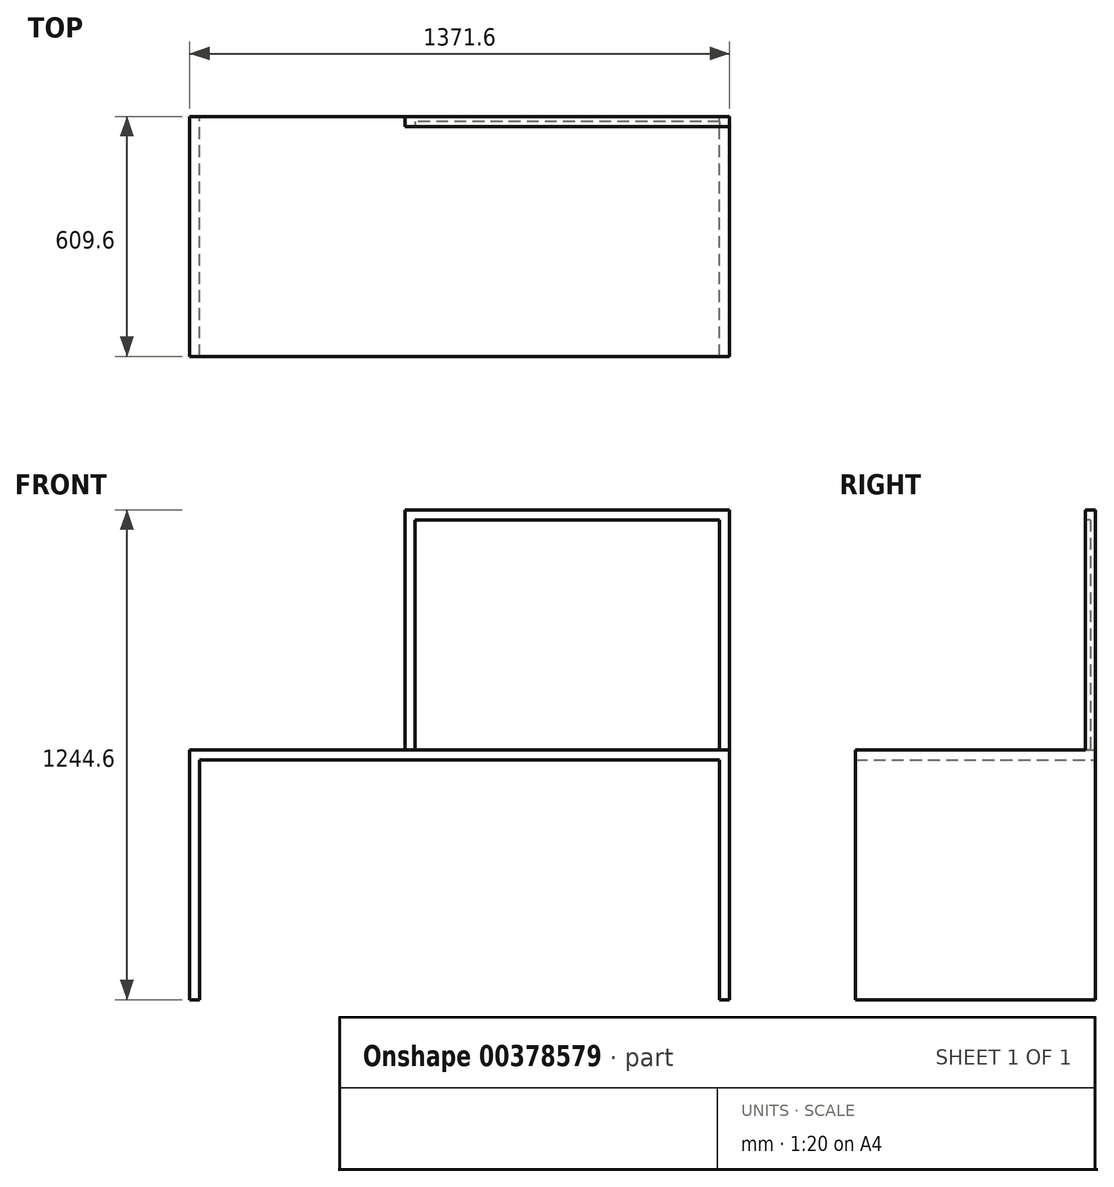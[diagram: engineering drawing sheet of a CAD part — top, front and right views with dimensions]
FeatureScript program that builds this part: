
annotation { "Feature Type Name" : "Feature", "Feature Type Description" : "" }
export const myFeature = defineFeature(function(context is Context, id is Id, definition is map)
    precondition{}
    {
        {
            var Q0;
            Q0=qCreatedBy(makeId("Top.planeOp"),FACE);
            var sketch = newSketch(context, id + "F0", { "sketchPlane" : qUnion([Q0])});
            skLineSegment(sketch, "E0.bottom", {"start": v(-674.96, -444.19) * mm, "end": v(696.64, -444.19) * mm});
            skLineSegment(sketch, "E0.top", {"start": v(-674.96, 165.41) * mm, "end": v(696.64, 165.41) * mm});
            skLineSegment(sketch, "E0.left", {"start": v(-674.96, -444.19) * mm, "end": v(-674.96, 165.41) * mm});
            skLineSegment(sketch, "E0.right", {"start": v(696.64, -444.19) * mm, "end": v(696.64, 165.41) * mm});
            skSolve(sketch);
        }
        {
            var Q0;
            Q0=makeQuery(id+"F0.imprint","IMPRINT",FACE,{"disambiguationData":[TD([[makeQuery(id+"F0.imprint","IMPRINT",EDGE,{"derivedFrom":sQuery(id+"F0.wireOp",EDGE,"E0.bottom")}),1.0]])]});
            extrude(context, id + "F1", {"entities" : qUnion([Q0]), "depth" : 25.4 * mm});
        }
        {
            var Q0;
            Q0=makeQuery(id+"F1.opExtrude","SWEPT_FACE",FACE,{"disambiguationData":[OSD([sQuery(id+"F0.wireOp",EDGE,"E0.right")])]});
            var sketch = newSketch(context, id + "F2", { "sketchPlane" : qUnion([Q0])});
            skLineSegment(sketch, "E1.bottom", {"start": v(-444.19, 25.4) * mm, "end": v(165.41, 25.4) * mm});
            skLineSegment(sketch, "E1.top", {"start": v(-444.19, -609.6) * mm, "end": v(165.41, -609.6) * mm});
            skLineSegment(sketch, "E1.left", {"start": v(-444.19, 25.4) * mm, "end": v(-444.19, -609.6) * mm});
            skLineSegment(sketch, "E1.right", {"start": v(165.41, 25.4) * mm, "end": v(165.41, -609.6) * mm});
            skSolve(sketch);
        }
        {
            var Q0;
            {var subQ0=sQuery(id+"F2.wireOp",EDGE,"E1.top");Q0=makeQuery(id+"F2.imprint","IMPRINT",FACE,{"disambiguationData":[TD([[makeQuery(id+"F2.imprint","IMPRINT",EDGE,{"derivedFrom":subQ0}),1.0]])]});}
            extrude(context, id + "F3", {"entities" : qUnion([Q0]), "operationType" : NewBodyOperationType.ADD, "oppositeDirection" : true, "depth" : 25.4 * mm});
        }
        {
            var Q0;
            Q0=makeQuery(id+"F1.opExtrude","SWEPT_FACE",FACE,{"disambiguationData":[OSD([sQuery(id+"F0.wireOp",EDGE,"E0.left")])]});
            var sketch = newSketch(context, id + "F4", { "sketchPlane" : qUnion([Q0])});
            skLineSegment(sketch, "E2.bottom", {"start": v(-165.41, 25.4) * mm, "end": v(444.19, 25.4) * mm});
            skLineSegment(sketch, "E2.top", {"start": v(-165.41, -609.6) * mm, "end": v(444.19, -609.6) * mm});
            skLineSegment(sketch, "E2.left", {"start": v(-165.41, 25.4) * mm, "end": v(-165.41, -609.6) * mm});
            skLineSegment(sketch, "E2.right", {"start": v(444.19, 25.4) * mm, "end": v(444.19, -609.6) * mm});
            skSolve(sketch);
        }
        {
            var Q0;
            {var subQ0=sQuery(id+"F4.wireOp",EDGE,"E2.top");Q0=makeQuery(id+"F4.imprint","IMPRINT",FACE,{"disambiguationData":[TD([[makeQuery(id+"F4.imprint","IMPRINT",EDGE,{"derivedFrom":subQ0}),1.0]])]});}
            extrude(context, id + "F5", {"entities" : qUnion([Q0]), "operationType" : NewBodyOperationType.ADD, "oppositeDirection" : true, "depth" : 25.4 * mm});
        }
        {
            var Q0;
            Q0=makeQuery(id+"F1.opExtrude","CAP_FACE",FACE,{"disambiguationData":[OSD([sQuery(id+"F0.wireOp",EDGE,"E0.bottom"),sQuery(id+"F0.wireOp",EDGE,"E0.top"),sQuery(id+"F0.wireOp",EDGE,"E0.left"),sQuery(id+"F0.wireOp",EDGE,"E0.right")])],"isStart":false});
            var sketch = newSketch(context, id + "F6", { "sketchPlane" : qUnion([Q0])});
            skLineSegment(sketch, "E3.bottom", {"start": v(696.64, 140.01) * mm, "end": v(-128.6, 140.01) * mm});
            skLineSegment(sketch, "E3.top", {"start": v(696.64, 165.41) * mm, "end": v(-128.6, 165.41) * mm});
            skLineSegment(sketch, "E3.left", {"start": v(696.64, 140.01) * mm, "end": v(696.64, 165.41) * mm});
            skLineSegment(sketch, "E3.right", {"start": v(-128.6, 140.01) * mm, "end": v(-128.6, 165.41) * mm});
            skSolve(sketch);
        }
        {
            var Q0;
            Q0=makeQuery(id+"F6.imprint","IMPRINT",FACE,{"disambiguationData":[TD([[makeQuery(id+"F6.imprint","IMPRINT",EDGE,{"derivedFrom":sQuery(id+"F6.wireOp",EDGE,"E3.bottom")}),-1.0]])]});
            extrude(context, id + "F7", {"entities" : qUnion([Q0]), "operationType" : NewBodyOperationType.ADD, "depth" : 609.6 * mm});
        }
        {
            var Q0;
            Q0=makeQuery(id+"F7.opExtrude","SWEPT_FACE",FACE,{"disambiguationData":[OSD([sQuery(id+"F6.wireOp",EDGE,"E3.bottom")])]});
            var sketch = newSketch(context, id + "F8", { "sketchPlane" : qUnion([Q0])});
            skLineSegment(sketch, "E4.bottom", {"start": v(-103.2, 609.6) * mm, "end": v(671.24, 609.6) * mm});
            skLineSegment(sketch, "E4.top", {"start": v(-103.2, 25.4) * mm, "end": v(671.24, 25.4) * mm});
            skLineSegment(sketch, "E4.left", {"start": v(-103.2, 609.6) * mm, "end": v(-103.2, 25.4) * mm});
            skLineSegment(sketch, "E4.right", {"start": v(671.24, 609.6) * mm, "end": v(671.24, 25.4) * mm});
            skSolve(sketch);
        }
        {
            var Q0;
            Q0=makeQuery(id+"F8.imprint","IMPRINT",FACE,{"disambiguationData":[TD([[makeQuery(id+"F8.imprint","IMPRINT",EDGE,{"derivedFrom":sQuery(id+"F8.wireOp",EDGE,"E4.bottom")}),-1.0]])]});
            extrude(context, id + "F9", {"entities" : qUnion([Q0]), "operationType" : NewBodyOperationType.REMOVE, "oppositeDirection" : true, "depth" : 12.7 * mm});
        }
    });
